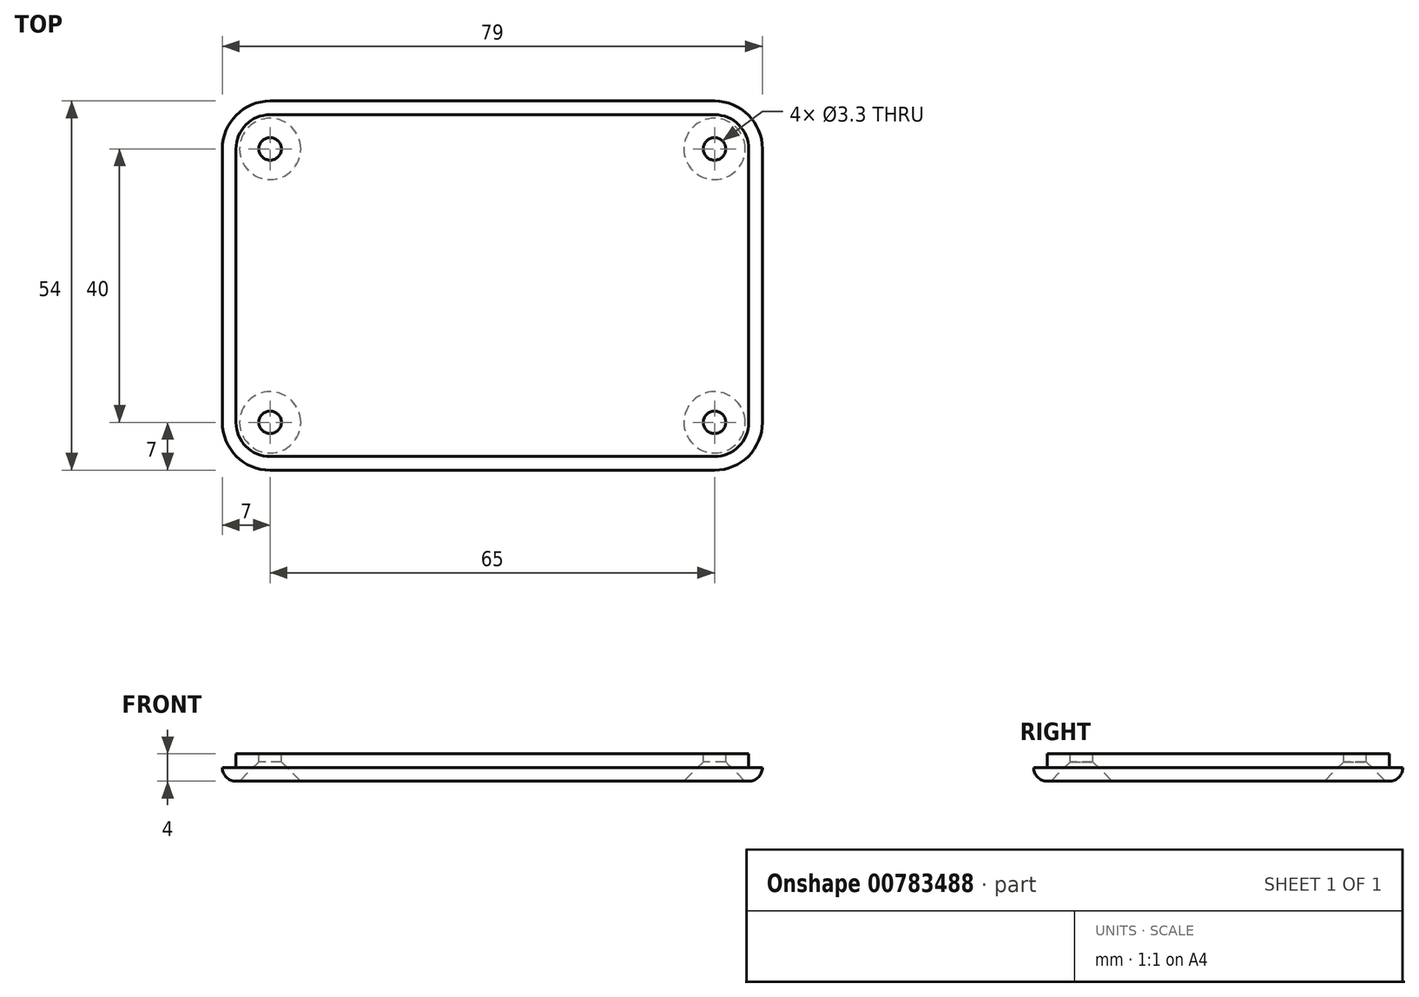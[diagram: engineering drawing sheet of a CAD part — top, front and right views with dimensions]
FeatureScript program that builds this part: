
annotation { "Feature Type Name" : "Feature", "Feature Type Description" : "" }
export const myFeature = defineFeature(function(context is Context, id is Id, definition is map)
    precondition{}
    {
        {
            var Q0;
            Q0=qCreatedBy(makeId("Top.planeOp"),FACE);
            var sketch = newSketch(context, id + "F0", { "sketchPlane" : qUnion([Q0])});
            skLineSegment(sketch, "E0.bottom", {"start": v(-32.5, 25) * mm, "end": v(32.5, 25) * mm});
            skLineSegment(sketch, "E0.top", {"start": v(-32.5, -25) * mm, "end": v(32.5, -25) * mm});
            skLineSegment(sketch, "E0.left", {"start": v(-37.5, 20) * mm, "end": v(-37.5, -20) * mm});
            skLineSegment(sketch, "E0.right", {"start": v(37.5, 20) * mm, "end": v(37.5, -20) * mm});
            skPoint(sketch, "E1.visualSharp", {"position": v(-37.5, 25) * mm});
            skArc(sketch, "E1.filletArc", {"start": v(-32.5, 25) * mm, "mid": v(-36.04, 23.54) * mm, "end": v(-37.5, 20) * mm});
            skPoint(sketch, "E2.visualSharp", {"position": v(37.5, 25) * mm});
            skArc(sketch, "E2.filletArc", {"start": v(37.5, 20) * mm, "mid": v(36.04, 23.54) * mm, "end": v(32.5, 25) * mm});
            skPoint(sketch, "E3.visualSharp", {"position": v(37.5, -25) * mm});
            skArc(sketch, "E3.filletArc", {"start": v(32.5, -25) * mm, "mid": v(36.04, -23.54) * mm, "end": v(37.5, -20) * mm});
            skPoint(sketch, "E4.visualSharp", {"position": v(-37.5, -25) * mm});
            skArc(sketch, "E4.filletArc", {"start": v(-37.5, -20) * mm, "mid": v(-36.04, -23.54) * mm, "end": v(-32.5, -25) * mm});
            skArc(sketch, "E5.0", {"start": v(-32.5, 27) * mm, "mid": v(-37.45, 24.95) * mm, "end": v(-39.5, 20) * mm});
            skLineSegment(sketch, "E5.1", {"start": v(-39.5, 20) * mm, "end": v(-39.5, -20) * mm});
            skLineSegment(sketch, "E5.2", {"start": v(-32.5, 27) * mm, "end": v(32.5, 27) * mm});
            skArc(sketch, "E5.3", {"start": v(-39.5, -20) * mm, "mid": v(-37.45, -24.95) * mm, "end": v(-32.5, -27) * mm});
            skArc(sketch, "E5.4", {"start": v(39.5, 20) * mm, "mid": v(37.45, 24.95) * mm, "end": v(32.5, 27) * mm});
            skLineSegment(sketch, "E5.5", {"start": v(39.5, 20) * mm, "end": v(39.5, -20) * mm});
            skArc(sketch, "E5.6", {"start": v(32.5, -27) * mm, "mid": v(37.45, -24.95) * mm, "end": v(39.5, -20) * mm});
            skLineSegment(sketch, "E5.7", {"start": v(-32.5, -27) * mm, "end": v(32.5, -27) * mm});
            skSolve(sketch);
        }
        {
            var Q0;
            Q0=makeQuery(id+"F0.imprint","IMPRINT",FACE,{"disambiguationData":[TD([[makeQuery(id+"F0.imprint","IMPRINT",EDGE,{"derivedFrom":sQuery(id+"F0.wireOp",EDGE,"E0.bottom")}),1.0]])]});
            var Q1;
            Q1=makeQuery(id+"F0.imprint","IMPRINT",FACE,{"disambiguationData":[TD([[makeQuery(id+"F0.imprint","IMPRINT",EDGE,{"derivedFrom":sQuery(id+"F0.wireOp",EDGE,"E0.bottom")}),-1.0]])]});
            extrude(context, id + "F1", {"entities" : qUnion([Q0, Q1]), "depth" : 2 * mm, "offsetDistance" : 25 * mm});
        }
        {
            var Q0;
            Q0=makeQuery(id+"F0.imprint","IMPRINT",FACE,{"disambiguationData":[TD([[makeQuery(id+"F0.imprint","IMPRINT",EDGE,{"derivedFrom":sQuery(id+"F0.wireOp",EDGE,"E0.bottom")}),-1.0]])]});
            extrude(context, id + "F2", {"entities" : qUnion([Q0]), "operationType" : NewBodyOperationType.ADD, "depth" : 4 * mm, "offsetDistance" : 25 * mm});
        }
        {
            var Q0;
            Q0=makeQuery(id+"F1.opExtrude","CAP_FACE",FACE,{"disambiguationData":[OSD([sQuery(id+"F0.wireOp",EDGE,"E5.0"),sQuery(id+"F0.wireOp",EDGE,"E5.1"),sQuery(id+"F0.wireOp",EDGE,"E5.2"),sQuery(id+"F0.wireOp",EDGE,"E5.3"),sQuery(id+"F0.wireOp",EDGE,"E5.4"),sQuery(id+"F0.wireOp",EDGE,"E5.5"),sQuery(id+"F0.wireOp",EDGE,"E5.6"),sQuery(id+"F0.wireOp",EDGE,"E5.7")])],"isStart":true});
            fillet(context, id + "F3", {"entities" : qUnion([Q0]), "radius" : 2 * mm, "tangentPropagation" : true, "allowEdgeOverflow" : false});
        }
        {
            var Q0;
            Q0=sQuery(id+"F0.wireOp",VERTEX,"E3.filletArc.center");
            var Q1;
            Q1=sQuery(id+"F0.wireOp",VERTEX,"E2.filletArc.center");
            var Q2;
            Q2=sQuery(id+"F0.wireOp",VERTEX,"E1.filletArc.center");
            var Q3;
            Q3=sQuery(id+"F0.wireOp",VERTEX,"E4.filletArc.center");
            var Q4;
            Q4=makeQuery(id+"F1.opExtrude","SWEPT_BODY",BODY,{"disambiguationData":[OSD([sQuery(id+"F0.wireOp",EDGE,"E5.0"),sQuery(id+"F0.wireOp",EDGE,"E5.1"),sQuery(id+"F0.wireOp",EDGE,"E5.2"),sQuery(id+"F0.wireOp",EDGE,"E5.3"),sQuery(id+"F0.wireOp",EDGE,"E5.4"),sQuery(id+"F0.wireOp",EDGE,"E5.5"),sQuery(id+"F0.wireOp",EDGE,"E5.6"),sQuery(id+"F0.wireOp",EDGE,"E5.7")])]});
            hole(context, id + "F4", {"style" : HoleStyle.C_SINK, "endStyle" : HoleEndStyle.THROUGH, "oppositeDirection" : true, "standardTappedOrClearance" : lookupTablePath({ "standard" : "ISO", "engagement" : "75%", "pitch" : "0.7 mm", "size" : "M4", "type" : "Tapped" }), "standardBlindInLast" : lookupTablePath({ "standard" : "ISO", "engagement" : "75%", "pitch" : "0.7 mm", "size" : "M4", "type" : "Tapped" }), "holeDiameter" : 3.3 * mm, "cSinkDiameter" : 8.96 * mm, "cSinkAngle" : 90 * degree, "majorDiameter" : 4 * mm, "showTappedDepth" : true, "isTappedThrough" : true, "tappedDepth" : 12 * mm, "tapClearance" : 3, "locations" : qUnion([Q0, Q1, Q2, Q3]), "scope" : qUnion([Q4])});
        }
    });
